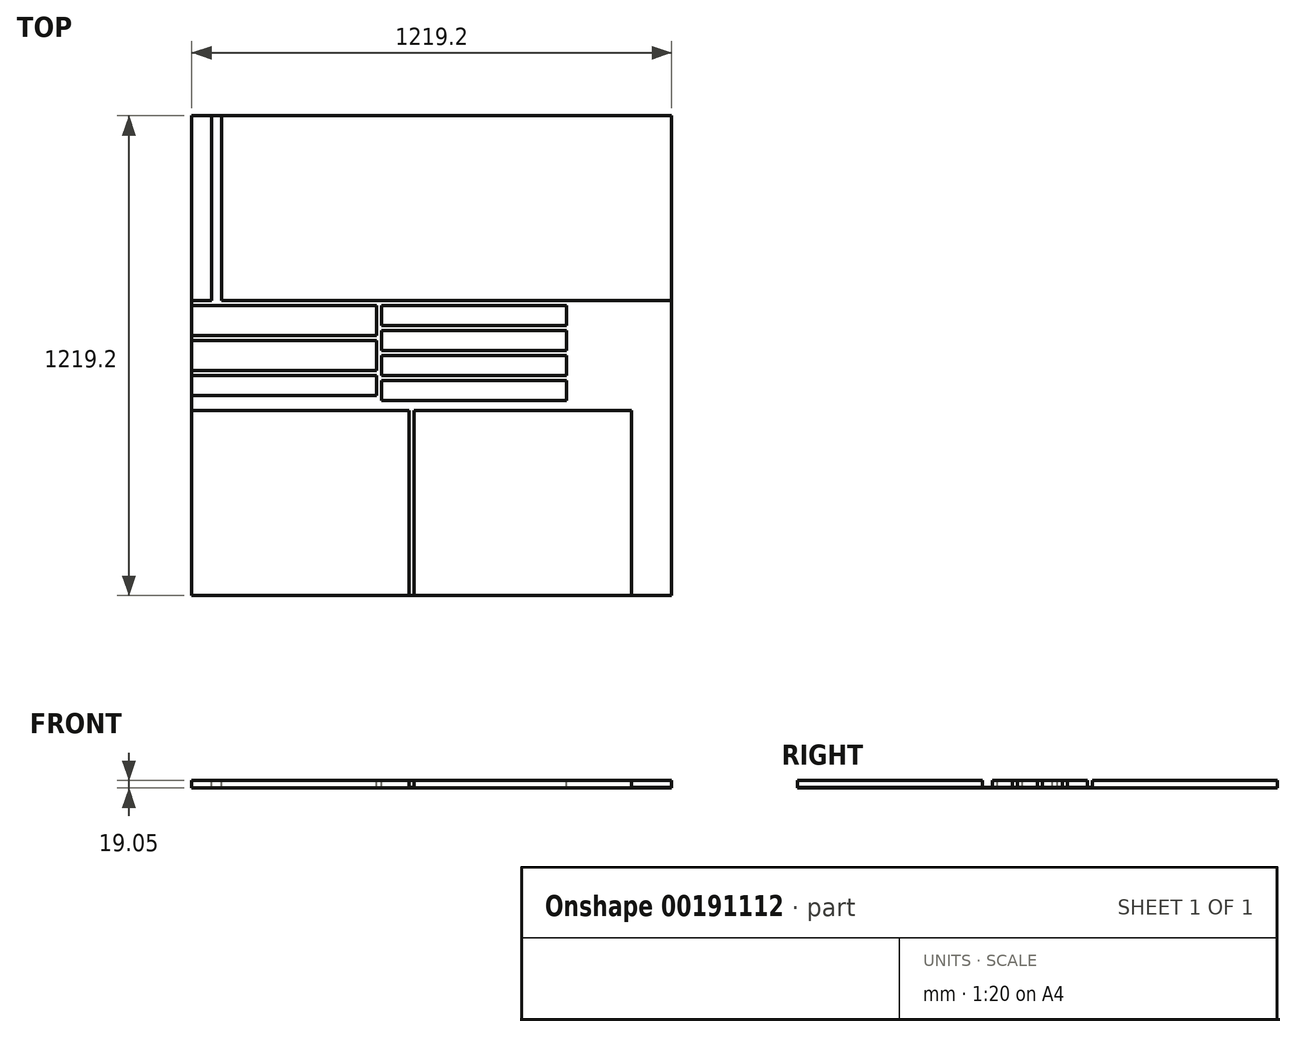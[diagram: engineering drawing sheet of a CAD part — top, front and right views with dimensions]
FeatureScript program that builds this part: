
annotation { "Feature Type Name" : "Feature", "Feature Type Description" : "" }
export const myFeature = defineFeature(function(context is Context, id is Id, definition is map)
    precondition{}
    {
        {
            var Q0;
            Q0=qCreatedBy(makeId("Top.planeOp"),FACE);
            var sketch = newSketch(context, id + "F0", { "sketchPlane" : qUnion([Q0])});
            skLineSegment(sketch, "E0.bottom", {"start": v(-609.6, 609.6) * mm, "end": v(609.6, 609.6) * mm});
            skLineSegment(sketch, "E0.top", {"start": v(-609.6, -609.6) * mm, "end": v(609.6, -609.6) * mm});
            skLineSegment(sketch, "E0.left", {"start": v(-609.6, 609.6) * mm, "end": v(-609.6, -609.6) * mm});
            skLineSegment(sketch, "E0.right", {"start": v(609.6, 609.6) * mm, "end": v(609.6, -609.6) * mm});
            skPoint(sketch, "E0.middle", {"position": v(0, 0) * mm});
            skSolve(sketch);
        }
        {
            var Q0;
            Q0 = qSketchRegion(id + "F0", true);
            extrude(context, id + "F1", {"entities" : qUnion([Q0]), "depth" : 19.05 * mm});
        }
        {
            var Q0;
            Q0=makeQuery(id+"F1.opExtrude","CAP_FACE",FACE,{"disambiguationData":[OSD([sQuery(id+"F0.wireOp",EDGE,"E0.bottom"),sQuery(id+"F0.wireOp",EDGE,"E0.top"),sQuery(id+"F0.wireOp",EDGE,"E0.left"),sQuery(id+"F0.wireOp",EDGE,"E0.right")])],"isStart":false});
            var sketch = newSketch(context, id + "F2", { "sketchPlane" : qUnion([Q0])});
            skLineSegment(sketch, "E1.bottom", {"start": v(-533.4, 609.6) * mm, "end": v(609.6, 609.6) * mm});
            skLineSegment(sketch, "E1.top", {"start": v(-533.4, 139.7) * mm, "end": v(609.6, 139.7) * mm});
            skLineSegment(sketch, "E1.left", {"start": v(-533.4, 609.6) * mm, "end": v(-533.4, 139.7) * mm});
            skLineSegment(sketch, "E1.right", {"start": v(609.6, 609.6) * mm, "end": v(609.6, 139.7) * mm});
            skLineSegment(sketch, "E2.bottom", {"start": v(-609.6, -139.7) * mm, "end": v(-57.15, -139.7) * mm});
            skLineSegment(sketch, "E2.top", {"start": v(-609.6, -609.6) * mm, "end": v(-57.15, -609.6) * mm});
            skLineSegment(sketch, "E2.left", {"start": v(-609.6, -139.7) * mm, "end": v(-609.6, -609.6) * mm});
            skLineSegment(sketch, "E2.right", {"start": v(-57.15, -139.7) * mm, "end": v(-57.15, -609.6) * mm});
            skLineSegment(sketch, "E3.bottom", {"start": v(-44.45, -139.7) * mm, "end": v(508, -139.7) * mm});
            skLineSegment(sketch, "E3.top", {"start": v(-44.45, -609.6) * mm, "end": v(508, -609.6) * mm});
            skLineSegment(sketch, "E3.left", {"start": v(-44.45, -139.7) * mm, "end": v(-44.45, -609.6) * mm});
            skLineSegment(sketch, "E3.right", {"start": v(508, -139.7) * mm, "end": v(508, -609.6) * mm});
            skLineSegment(sketch, "E4.bottom", {"start": v(-609.6, 127) * mm, "end": v(-139.7, 127) * mm});
            skLineSegment(sketch, "E4.top", {"start": v(-609.6, 50.8) * mm, "end": v(-139.7, 50.8) * mm});
            skLineSegment(sketch, "E4.left", {"start": v(-609.6, 127) * mm, "end": v(-609.6, 50.8) * mm});
            skLineSegment(sketch, "E4.right", {"start": v(-139.7, 127) * mm, "end": v(-139.7, 50.8) * mm});
            skLineSegment(sketch, "E5.bottom", {"start": v(-609.6, 38.1) * mm, "end": v(-139.7, 38.1) * mm});
            skLineSegment(sketch, "E5.top", {"start": v(-609.6, -38.1) * mm, "end": v(-139.7, -38.1) * mm});
            skLineSegment(sketch, "E5.left", {"start": v(-609.6, 38.1) * mm, "end": v(-609.6, -38.1) * mm});
            skLineSegment(sketch, "E5.right", {"start": v(-139.7, 38.1) * mm, "end": v(-139.7, -38.1) * mm});
            skLineSegment(sketch, "E6.bottom", {"start": v(-127, 127) * mm, "end": v(342.9, 127) * mm});
            skLineSegment(sketch, "E6.top", {"start": v(-127, 76.2) * mm, "end": v(342.9, 76.2) * mm});
            skLineSegment(sketch, "E6.left", {"start": v(-127, 127) * mm, "end": v(-127, 76.2) * mm});
            skLineSegment(sketch, "E6.right", {"start": v(342.9, 127) * mm, "end": v(342.9, 76.2) * mm});
            skLineSegment(sketch, "E7.bottom", {"start": v(-127, 63.5) * mm, "end": v(342.9, 63.5) * mm});
            skLineSegment(sketch, "E7.top", {"start": v(-127, 12.7) * mm, "end": v(342.9, 12.7) * mm});
            skLineSegment(sketch, "E7.left", {"start": v(-127, 63.5) * mm, "end": v(-127, 12.7) * mm});
            skLineSegment(sketch, "E7.right", {"start": v(342.9, 63.5) * mm, "end": v(342.9, 12.7) * mm});
            skLineSegment(sketch, "E8.bottom", {"start": v(-127, 0) * mm, "end": v(342.9, 0) * mm});
            skLineSegment(sketch, "E8.top", {"start": v(-127, -50.8) * mm, "end": v(342.9, -50.8) * mm});
            skLineSegment(sketch, "E8.left", {"start": v(-127, 0) * mm, "end": v(-127, -50.8) * mm});
            skLineSegment(sketch, "E8.right", {"start": v(342.9, 0) * mm, "end": v(342.9, -50.8) * mm});
            skLineSegment(sketch, "E9.bottom", {"start": v(-609.6, -50.8) * mm, "end": v(-139.7, -50.8) * mm});
            skLineSegment(sketch, "E9.top", {"start": v(-609.6, -101.6) * mm, "end": v(-139.7, -101.6) * mm});
            skLineSegment(sketch, "E9.left", {"start": v(-609.6, -50.8) * mm, "end": v(-609.6, -101.6) * mm});
            skLineSegment(sketch, "E9.right", {"start": v(-139.7, -50.8) * mm, "end": v(-139.7, -101.6) * mm});
            skLineSegment(sketch, "E10.bottom", {"start": v(-127, -63.5) * mm, "end": v(342.9, -63.5) * mm});
            skLineSegment(sketch, "E10.top", {"start": v(-127, -114.3) * mm, "end": v(342.9, -114.3) * mm});
            skLineSegment(sketch, "E10.left", {"start": v(-127, -63.5) * mm, "end": v(-127, -114.3) * mm});
            skLineSegment(sketch, "E10.right", {"start": v(342.9, -63.5) * mm, "end": v(342.9, -114.3) * mm});
            skLineSegment(sketch, "E11.bottom", {"start": v(-609.6, 609.6) * mm, "end": v(-558.8, 609.6) * mm});
            skLineSegment(sketch, "E11.top", {"start": v(-609.6, 139.7) * mm, "end": v(-558.8, 139.7) * mm});
            skLineSegment(sketch, "E11.left", {"start": v(-609.6, 609.6) * mm, "end": v(-609.6, 139.7) * mm});
            skLineSegment(sketch, "E11.right", {"start": v(-558.8, 609.6) * mm, "end": v(-558.8, 139.7) * mm});
            skSolve(sketch);
        }
        {
            var Q0;
            {var subQ11=sQuery(id+"F2.wireOp",EDGE,"E1.top");Q0=makeQuery(id+"F2.imprint","IMPRINT",FACE,{"disambiguationData":[TD([[makeQuery(id+"F2.imprint","IMPRINT",EDGE,{"derivedFrom":subQ11}),-1.0]])]});}
            extrude(context, id + "F3", {"entities" : qUnion([Q0]), "operationType" : NewBodyOperationType.REMOVE, "oppositeDirection" : true, "depth" : 17.14 * mm});
        }
    });
